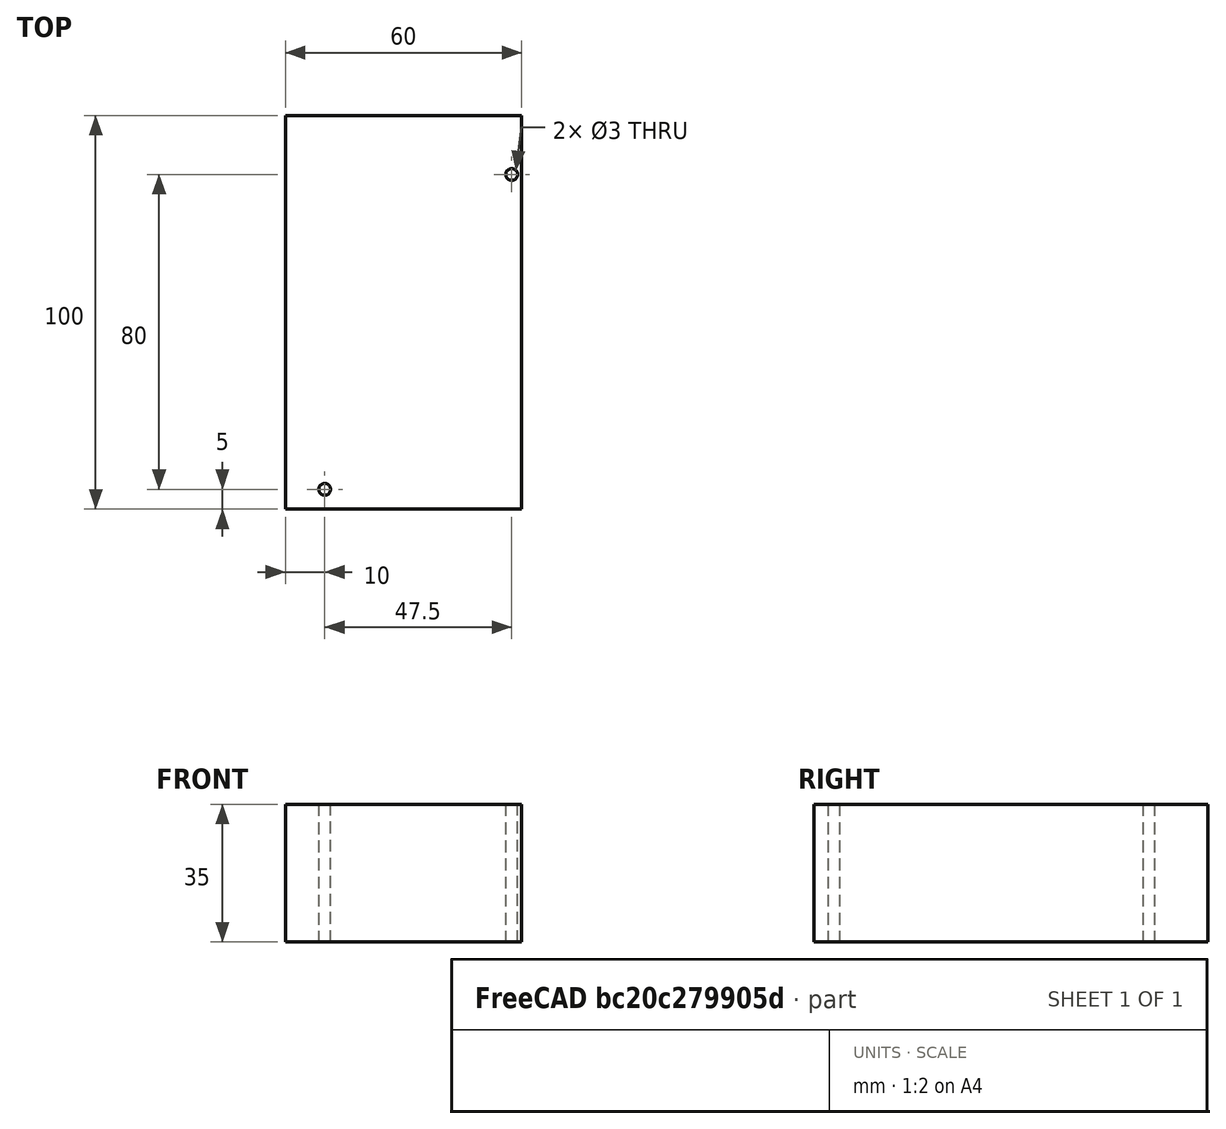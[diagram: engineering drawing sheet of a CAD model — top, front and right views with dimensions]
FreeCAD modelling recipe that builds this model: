
FCSTD DOCUMENT  (FreeCAD 0.18R14555 (Git shallow))
Label: ramps-controller
License: All rights reserved
LicenseURL: http://en.wikipedia.org/wiki/All_rights_reserved
objects: Sketcher::SketchObject×1, PartDesign::Pad×1, PartDesign::Body×1
note: 4 computed .brp shape members not serialized (recipe doc carries the construction recipe); baked Part::Feature solids carry a one-line shape summary decoded from their .brp

FEATURE [Sketcher::SketchObject] Sketch
  MapMode = 5
  Support = -> [XY_Plane]
  sketch-geometry (6):
    g0: LineSegment StartX=0 StartY=0 StartZ=0 EndX=60 EndY=0 EndZ=0
    g1: LineSegment StartX=60 StartY=0 StartZ=0 EndX=60 EndY=100 EndZ=0
    g2: LineSegment StartX=60 StartY=100 StartZ=0 EndX=0 EndY=100 EndZ=0
    g3: LineSegment StartX=0 StartY=100 StartZ=0 EndX=0 EndY=0 EndZ=0
    g4: Circle CenterX=10 CenterY=5 CenterZ=0 NormalX=0 NormalY=0 NormalZ=1 AngleXU=0 Radius=1.5
    g5: Circle CenterX=57.5 CenterY=85 CenterZ=0 NormalX=0 NormalY=0 NormalZ=1 AngleXU=0 Radius=1.5
  constraints (17):
    c: Coincident(g0,g1)
    c: Coincident(g1,g2)
    c: Coincident(g2,g3)
    c: Coincident(g3,g0)
    c: Horizontal(g0)
    c: Horizontal(g2)
    c: Vertical(g1)
    c: Vertical(g3)
    c: Coincident(g0,g-1)
    c: Equal(g5,g4)
    c: DistanceX(g2,g2) = 60
    c: DistanceY(g1,g1) = 100
    c: DistanceX(g0,g4) = 10
    c: DistanceY(g0,g4) = 5
    c: Radius(g4) = 1.5
    c: DistanceY(g5,g1) = 15
    c: DistanceX(g5,g1) = 2.5
FEATURE [PartDesign::Pad] Pad
  Length = 35
  Length2 = 100
  Profile = -> Sketch
  Type = 0
FEATURE [PartDesign::Body] Body
  Group = -> [Sketch,Pad]
  Origin = -> Origin
  Tip = -> Pad
